# Revit family: Single_Fountain_Non-Filtered_Non-Refrigerated_Stainless-EDFP214C
name_source: partatom
category: Plumbing Fixtures
units: mm (PartAtom-declared; Revit-internal decimal feet)

## family parameters
Cut with Voids When Loaded = No
Host = Face
Maintain Annotation Orientation = No
OmniClass Number = 23.65.70.14.11
OmniClass Title = Drinking Fountains/Coolers
Part Type = Normal
Room Calculation Point = No
Round Connector Dimension = Use Diameter
Shared = No

## types (1)
- EDFP214C (Single Fountain Non-Filtered Non-Refrigerated Stainless)
    Activation Method = Mechanical Front Bubbler Button
    Approx. Shipping Weight (lbs) = 16
    Assembly Code = D2010
    Base_Height = 27 "
    Basing_Height = 6.5 "
    CW Connection = No
    Chilling Capacity (GPH) = 0
    Connection Outlet B = 0.25 "
    Connection Supply A = 0.38 "
    Default Elevation = 48 "
    Description = Soft Sides® Single ADA Fountain Non-Filtered Non-Refrigerated Stainless
    Dimensions (L x W x H) = 12 1/8 inch x 18 3/4 inch x 6 1/2 inch
    HW Connection = No
    Inlet Connection Size (inch) = 0.375
    Installation Location = Indoor
    Main Material = Finish-Elkay-Stainless Steel
    Manufacturer = Elkay Manufacturer Company
    Manufacturer Brand = Elkay (by Zurn Elkay Water Solutions)
    Model = EDFP214C
    Mounting Type = Wall Mount (Inwall Frame/Plate)
    Outlet connection Size (inch) = 1.25 "
    Product Documentation Link = https://www.elkayfiles.com
    Product Installation Sheet URL = https://www.elkayfiles.com
    Product Page URL = https://www.elkay.com
    Product Weight (lbs) = 14
    Product data URL = https://www.bimobject.com
    Repair Parts URL = https://www.elkayfiles.com
    URL = https://www.elkay.com
    Vent Connection = No
    Ventilation Angle = 83.99°
    Waste Connection = No

## geometry (parser evidence)
native form markers: Sweep x8
no freeform markers — native parametric forms only
